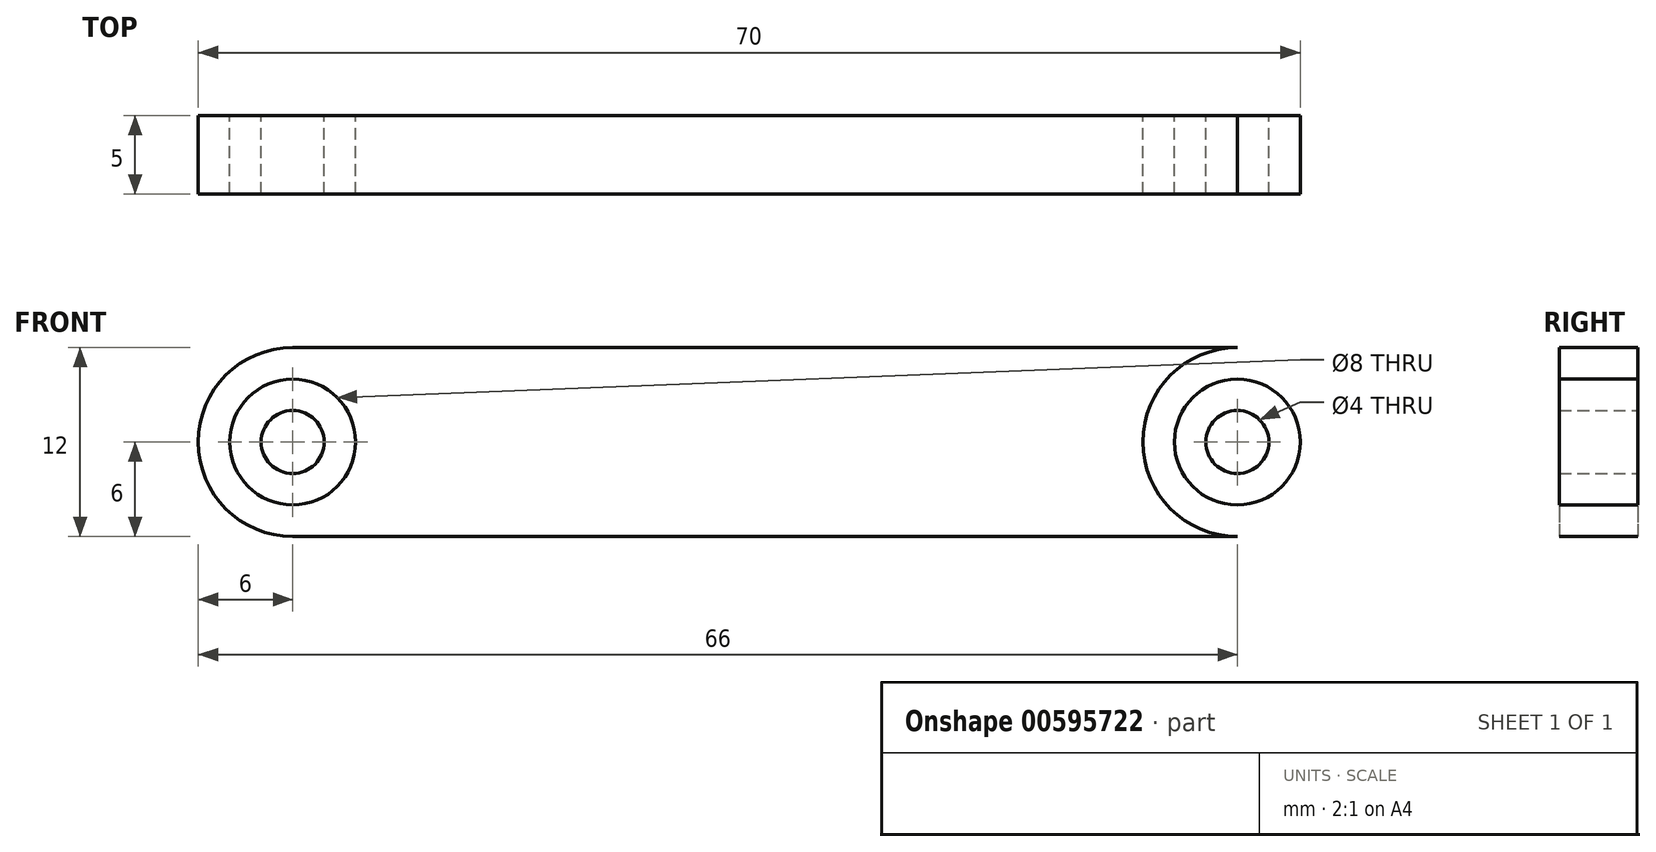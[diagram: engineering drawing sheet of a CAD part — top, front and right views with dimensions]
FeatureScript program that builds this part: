
annotation { "Feature Type Name" : "Feature", "Feature Type Description" : "" }
export const myFeature = defineFeature(function(context is Context, id is Id, definition is map)
    precondition{}
    {
        {
            var Q0;
            Q0=qCreatedBy(makeId("Front.planeOp"),FACE);
            var sketch = newSketch(context, id + "F0", { "sketchPlane" : qUnion([Q0])});
            skCircle(sketch, "E0", {"center": v(-30, 0) * mm, "radius": 2 * mm});
            skCircle(sketch, "E1", {"center": v(-30, 0) * mm, "radius": 4 * mm});
            skCircle(sketch, "E2", {"center": v(-30, 0) * mm, "radius": 6 * mm});
            skLineSegment(sketch, "E3", {"start": v(-30, 6) * mm, "end": v(0, 6) * mm});
            skLineSegment(sketch, "E4", {"start": v(-30, -6) * mm, "end": v(0, -6) * mm});
            skCircle(sketch, "E5.MirrorC", {"center": v(30, 0) * mm, "radius": 2 * mm});
            skCircle(sketch, "E6.MirrorC", {"center": v(30, 0) * mm, "radius": 4 * mm});
            skCircle(sketch, "E7.MirrorC", {"center": v(30, 0) * mm, "radius": 6 * mm});
            skLineSegment(sketch, "E8.MirrorCS", {"start": v(30, 6) * mm, "end": v(0, 6) * mm});
            skLineSegment(sketch, "E9.MirrorCS", {"start": v(30, -6) * mm, "end": v(0, -6) * mm});
            skSolve(sketch);
        }
        {
            var Q0;
            {var subQ4=sQuery(id+"F0.wireOp",EDGE,"E3");Q0=makeQuery(id+"F0.imprint","IMPRINT",FACE,{"disambiguationData":[TD([[makeQuery(id+"F0.imprint","IMPRINT",EDGE,{"derivedFrom":subQ4}),-1.0]])]});}
            var Q1;
            Q1=makeQuery(id+"F0.imprint","IMPRINT",FACE,{"disambiguationData":[TD([[makeQuery(id+"F0.imprint","IMPRINT",EDGE,{"derivedFrom":sQuery(id+"F0.wireOp",EDGE,"E6.MirrorC")}),1.0]])]});
            var Q2;
            Q2=makeQuery(id+"F0.imprint","IMPRINT",FACE,{"disambiguationData":[TD([[makeQuery(id+"F0.imprint","IMPRINT",EDGE,{"derivedFrom":sQuery(id+"F0.wireOp",EDGE,"E5.MirrorC")}),-1.0]])]});
            var Q3;
            Q3=makeQuery(id+"F0.imprint","IMPRINT",FACE,{"disambiguationData":[TD([[makeQuery(id+"F0.imprint","IMPRINT",EDGE,{"derivedFrom":sQuery(id+"F0.wireOp",EDGE,"E1")}),-1.0]])]});
            var Q4;
            Q4=makeQuery(id+"F0.imprint","IMPRINT",FACE,{"disambiguationData":[TD([[makeQuery(id+"F0.imprint","IMPRINT",EDGE,{"derivedFrom":sQuery(id+"F0.wireOp",EDGE,"E0")}),1.0]])]});
            extrude(context, id + "F1", {"entities" : qUnion([Q0, Q1, Q2, Q3, Q4]), "depth" : 5 * mm, "offsetDistance" : 25 * mm});
        }
    });
